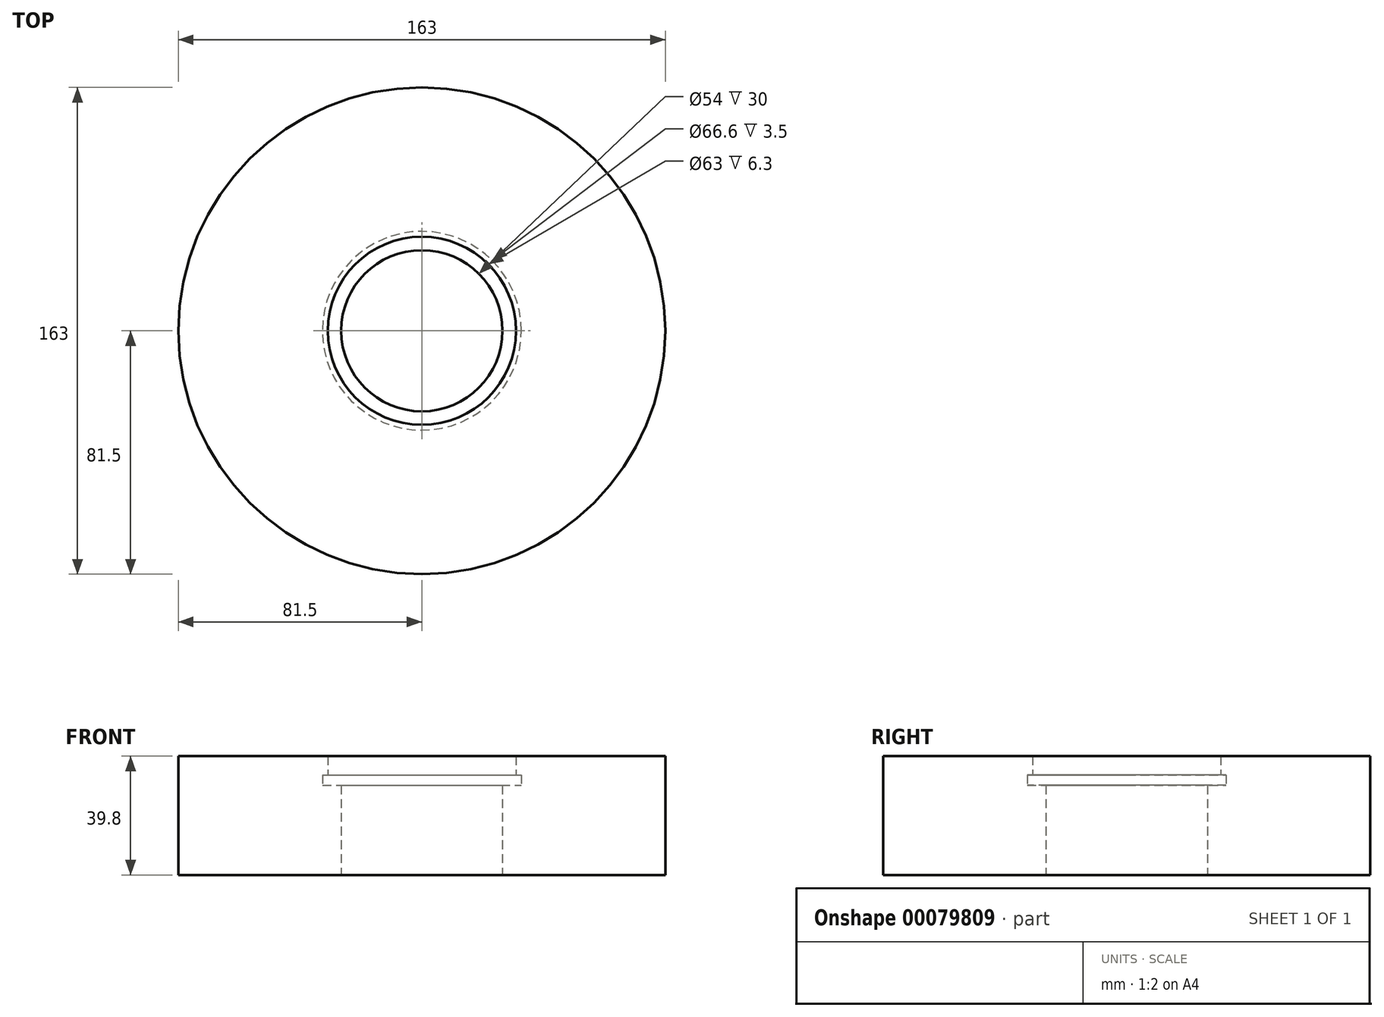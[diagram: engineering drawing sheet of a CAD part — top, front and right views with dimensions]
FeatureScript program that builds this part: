
annotation { "Feature Type Name" : "Feature", "Feature Type Description" : "" }
export const myFeature = defineFeature(function(context is Context, id is Id, definition is map)
    precondition{}
    {
        {
            var Q0;
            Q0=qCreatedBy(makeId("Front.planeOp"),FACE);
            var sketch = newSketch(context, id + "F0", { "sketchPlane" : qUnion([Q0])});
            skLineSegment(sketch, "E0", {"start": v(-81.5, 39.8) * mm, "end": v(-31.5, 39.8) * mm});
            skLineSegment(sketch, "E1", {"start": v(-31.5, 39.8) * mm, "end": v(-31.5, 33.5) * mm});
            skLineSegment(sketch, "E2", {"start": v(-31.5, 33.5) * mm, "end": v(-33.3, 33.5) * mm});
            skLineSegment(sketch, "E3", {"start": v(-33.3, 33.5) * mm, "end": v(-33.3, 30) * mm});
            skLineSegment(sketch, "E4", {"start": v(-33.3, 30) * mm, "end": v(-27, 30) * mm});
            skLineSegment(sketch, "E5", {"start": v(-27, 30) * mm, "end": v(-27, 0) * mm});
            skLineSegment(sketch, "E6", {"start": v(-27, 0) * mm, "end": v(-81.5, 0) * mm});
            skLineSegment(sketch, "E7", {"start": v(-81.5, 0) * mm, "end": v(-81.5, 39.8) * mm});
            skSolve(sketch);
        }
        {
            var Q0;
            Q0=qCreatedBy(makeId("Front.planeOp"),FACE);
            var sketch = newSketch(context, id + "F3", { "sketchPlane" : qUnion([Q0])});
            skLineSegment(sketch, "E8", {"start": v(0, 0) * mm, "end": v(0, 74.72) * mm});
            skSolve(sketch);
        }
        {
            var Q0;
            Q0=makeQuery(id+"F0.imprint","IMPRINT",FACE,{"disambiguationData":[TD([[makeQuery(id+"F0.imprint","IMPRINT",EDGE,{"derivedFrom":sQuery(id+"F0.wireOp",EDGE,"E0")}),-1.0]])]});
            var Q1;
            Q1=sQuery(id+"F3.wireOp",EDGE,"E8");
            revolve(context, id + "F4", {"entities" : qUnion([Q0]), "axis" : qUnion([Q1]), "revolveType" : RevolveType.FULL});
        }
    });
